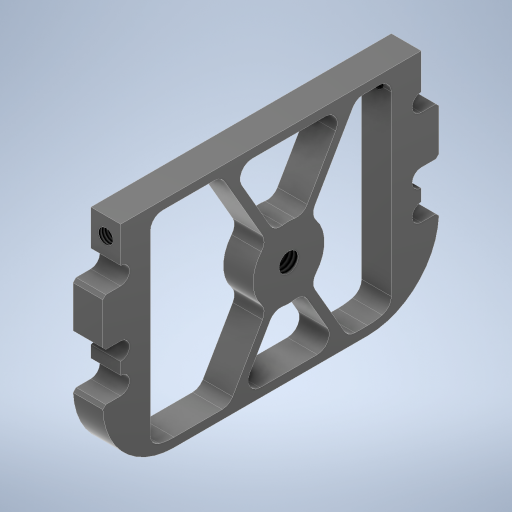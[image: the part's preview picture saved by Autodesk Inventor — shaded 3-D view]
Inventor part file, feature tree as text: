
AUTODESK INVENTOR PART (.ipt)
format: ipt  version: 2024.2 (Build 282272000, 272)  size: 450,048 bytes
history: native  units: mm
features: other x1, extrude x1, chamfer x1, hole x1, plane x1, mirror x1, sketch x1
ambient origin geometry x8: Origin, YZ Plane, XZ Plane, XY Plane, X Axis, Y Axis, Z Axis, Center Point
bodies: Solid1 (feature_tree)
feature tree (7):
  other  "UpperArmSideFrameBasis.ipt"
  extrude  "Extrusion1"  Depth=2.0mm TaperAngle=0.0deg
  chamfer  "Chamfer1"  Distance=2.0mm Angle=45.0deg
  hole  "Side-M3"  [1 undecoded]
  plane  "Work Plane1"
  mirror  "Mirror1"
  sketch  "Sketch1"  dims[d0=10.0mm d1=5.0mm d2=0.0mm d17=0.5mm d18=2.0mm d19=45.0deg d27=3.242mm d28=8.0mm d29=4.0mm d30=2.0mm d31=90.0deg d32=8.0mm d33=0.0mm d50=2.0mm d51=2.459mm d52=6.0mm d53=4.0mm d54=2.0mm d55=90.0deg d56=6.0mm d57=0.0mm d34=0.5mm d35=0.872665mm d36=0.5mm d37=0.872665mm]
note: 1 required parameter value undecoded (feature->parameter linkage not recoverable at this tier; creation-order binding heuristic only, values carry confidence <= 0.55)
